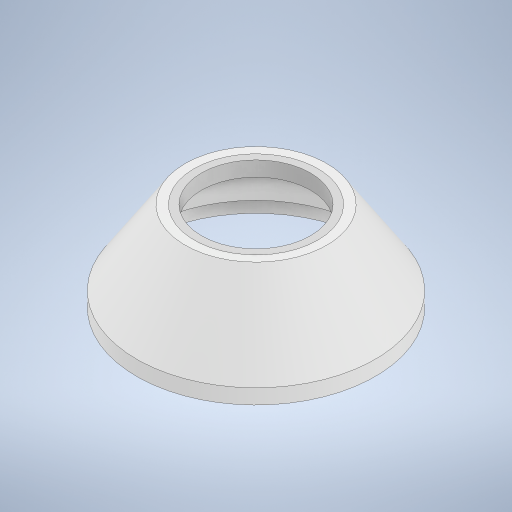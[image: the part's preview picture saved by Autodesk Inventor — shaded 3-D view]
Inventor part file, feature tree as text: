
AUTODESK INVENTOR PART (.ipt)
format: ipt  version: 2023 (Build 270158000, 158)  size: 615,424 bytes
history: native  units: mm
features: sketch x3, extrude x2, plane x1, loft x1, shell x1, other x1
ambient origin geometry x8: Origin, YZ Plane, XZ Plane, XY Plane, X Axis, Y Axis, Z Axis, Center Point
bodies: Solid1 (feature_tree)
feature tree (9):
  sketch  "Sketch1"  dims[d0=160.0mm d1=2.5mm]
  extrude  "Extrusion1"  Depth=2.5mm
  plane  "Work Plane1"
  loft  "Loft1"
  shell  "Shell1"  Thickness=25.0mm
  extrude  "Extrusion4"  TaperAngle=0.0deg  [1 undecoded]
  sketch  "Sketch2"  dims[d2=10.0mm d3=0.0mm d4=50.0mm d5=25.0mm]
  other  "Edges1"
  sketch  "Sketch4"  dims[d6=5.0mm d7=0.0mm d8=90.0deg d9=0.0mm d10=90.0deg d11=5.0mm d18=5.0mm d19=10.0mm d20=0.0mm]
note: 1 required parameter value undecoded (feature->parameter linkage not recoverable at this tier; creation-order binding heuristic only, values carry confidence <= 0.55)
